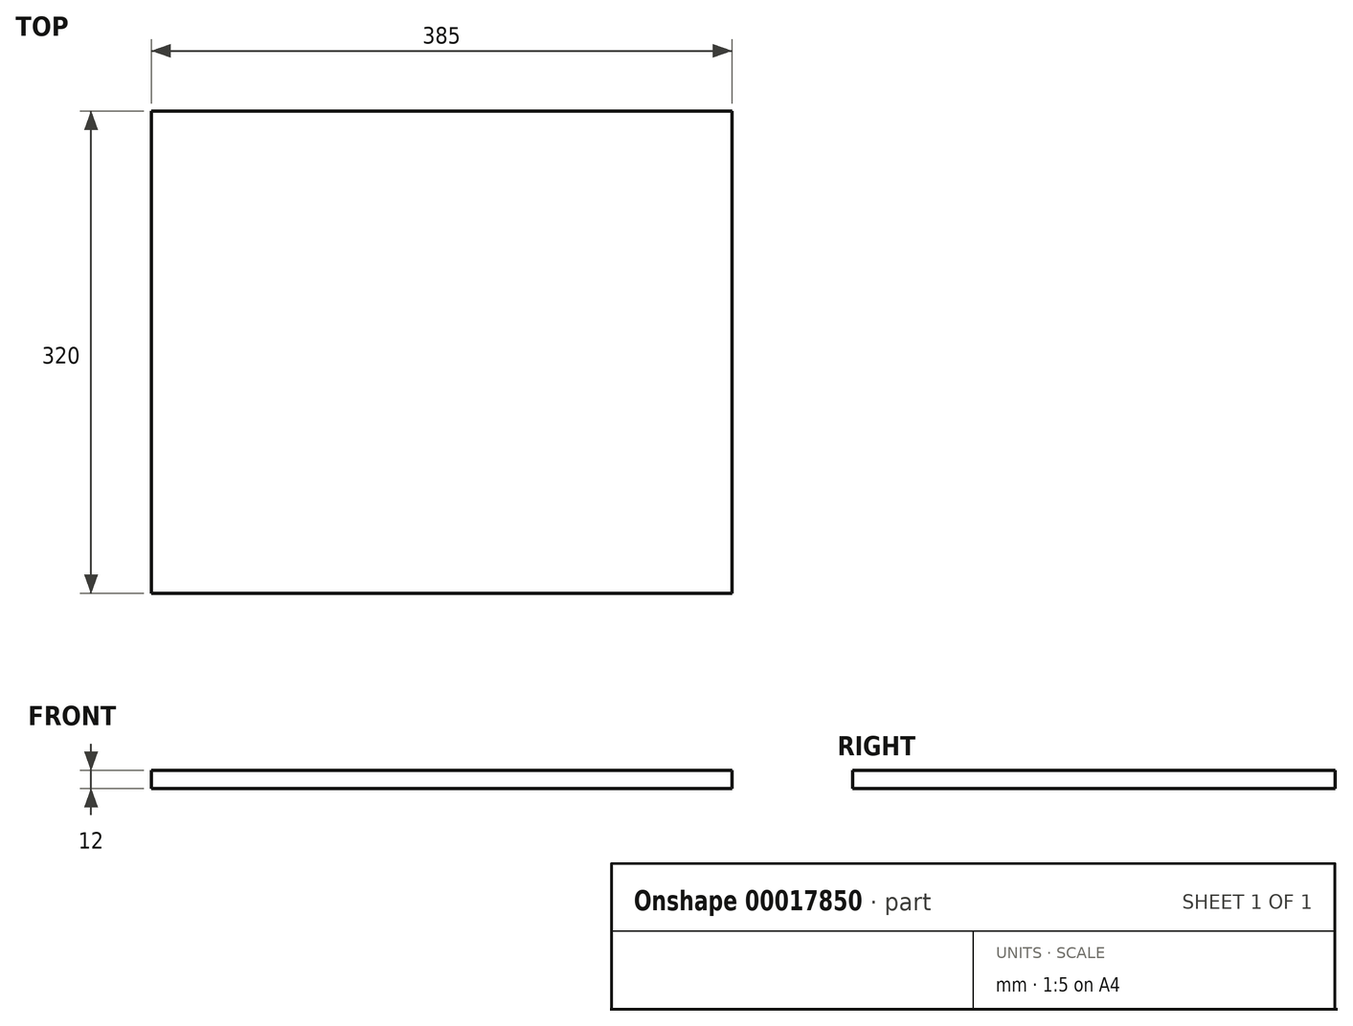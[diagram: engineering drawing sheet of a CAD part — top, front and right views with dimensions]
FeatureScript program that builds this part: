
annotation { "Feature Type Name" : "Feature", "Feature Type Description" : "" }
export const myFeature = defineFeature(function(context is Context, id is Id, definition is map)
    precondition{}
    {
        {
            var Q0;
            Q0=qCreatedBy(makeId("Top.planeOp"),FACE);
            var sketch = newSketch(context, id + "F0", { "sketchPlane" : qUnion([Q0])});
            skLineSegment(sketch, "E0.bottom", {"start": v(-70.96, 65.05) * mm, "end": v(314.04, 65.05) * mm});
            skLineSegment(sketch, "E0.top", {"start": v(-70.96, -254.95) * mm, "end": v(314.04, -254.95) * mm});
            skLineSegment(sketch, "E0.left", {"start": v(-70.96, 65.05) * mm, "end": v(-70.96, -254.95) * mm});
            skLineSegment(sketch, "E0.right", {"start": v(314.04, 65.05) * mm, "end": v(314.04, -254.95) * mm});
            skSolve(sketch);
        }
        {
            var Q0;
            Q0=qSketchRegion(id+"F0",true);
            extrude(context, id + "F1", {"entities" : qUnion([Q0]), "depth" : 12 * mm});
        }
    });
